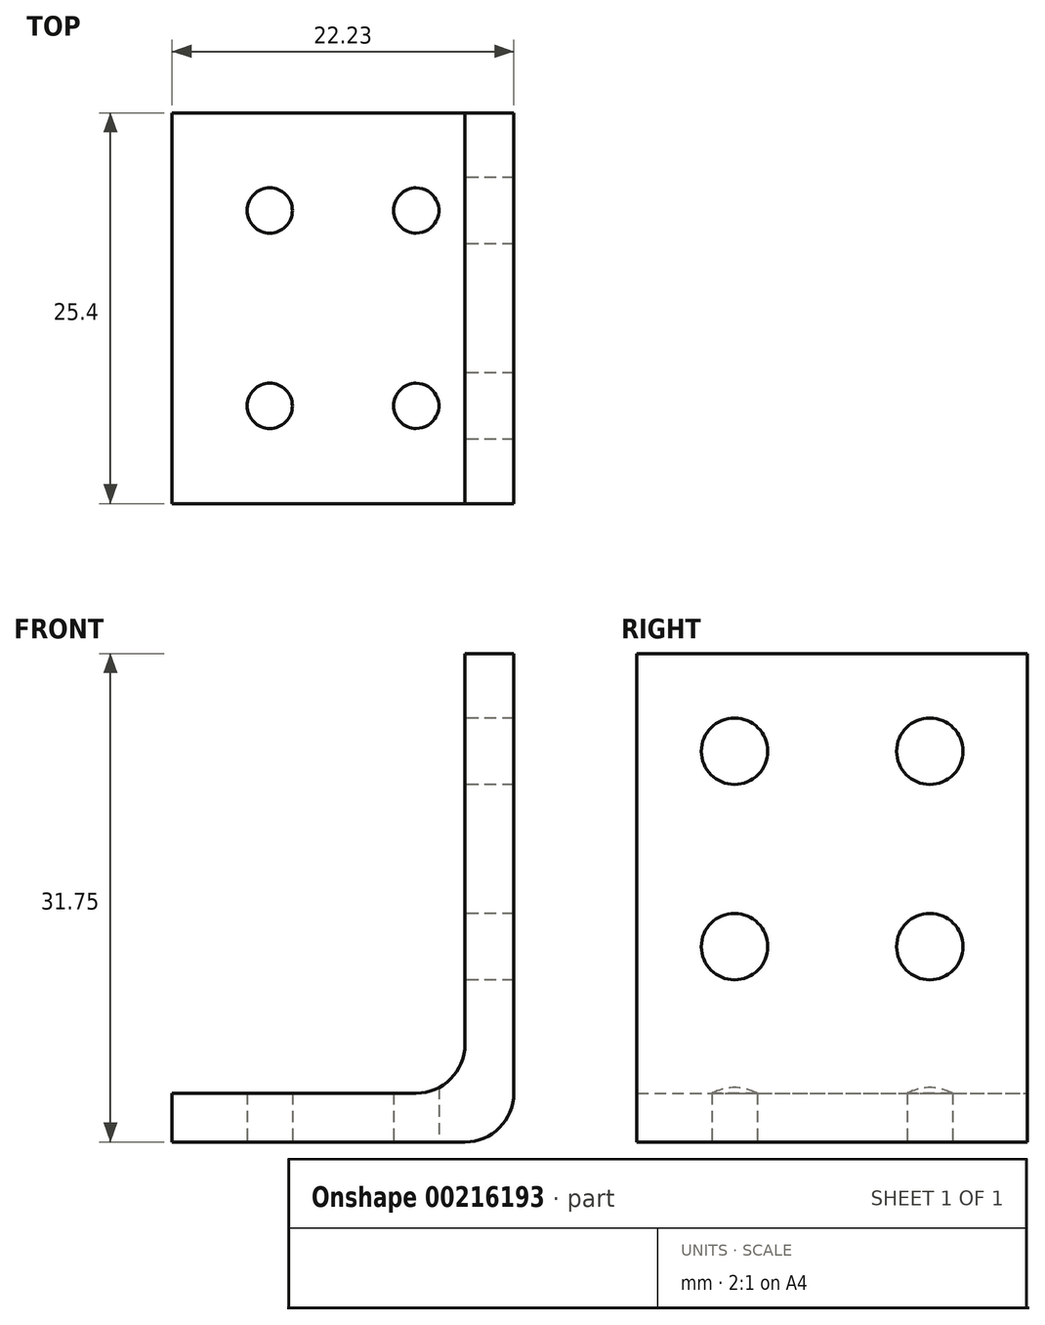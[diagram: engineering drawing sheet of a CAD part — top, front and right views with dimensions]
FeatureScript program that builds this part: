
annotation { "Feature Type Name" : "Feature", "Feature Type Description" : "" }
export const myFeature = defineFeature(function(context is Context, id is Id, definition is map)
    precondition{}
    {
        {
            var Q0;
            Q0=qCreatedBy(makeId("Front.planeOp"),FACE);
            var sketch = newSketch(context, id + "F0", { "sketchPlane" : qUnion([Q0])});
            skLineSegment(sketch, "E0", {"start": v(0, 3.18) * mm, "end": v(0, 31.75) * mm});
            skLineSegment(sketch, "E1", {"start": v(0, 31.75) * mm, "end": v(-3.17, 31.75) * mm});
            skLineSegment(sketch, "E2", {"start": v(-3.17, 31.75) * mm, "end": v(-3.17, 6.35) * mm});
            skLineSegment(sketch, "E3", {"start": v(-6.35, 3.17) * mm, "end": v(-22.22, 3.17) * mm});
            skLineSegment(sketch, "E4", {"start": v(-22.22, 3.17) * mm, "end": v(-22.22, 0) * mm});
            skLineSegment(sketch, "E5", {"start": v(-22.22, 0) * mm, "end": v(-3.17, 0) * mm});
            skPoint(sketch, "E6.visualSharp", {"position": v(-3.17, 3.17) * mm});
            skArc(sketch, "E6.filletArc", {"start": v(-6.35, 3.17) * mm, "mid": v(-4.1, 4.1) * mm, "end": v(-3.17, 6.35) * mm});
            skPoint(sketch, "E7.visualSharp", {"position": v(0, 0) * mm});
            skArc(sketch, "E7.filletArc", {"start": v(-3.17, 0) * mm, "mid": v(-0.93, 0.93) * mm, "end": v(0, 3.18) * mm});
            skSolve(sketch);
        }
        {
            var Q0;
            Q0=makeQuery(id+"F0.imprint","IMPRINT",FACE,{"disambiguationData":[TD([[makeQuery(id+"F0.imprint","IMPRINT",EDGE,{"derivedFrom":sQuery(id+"F0.wireOp",EDGE,"E0")}),1.0]])]});
            extrude(context, id + "F1", {"entities" : qUnion([Q0]), "depth" : 25.4 * mm});
        }
        {
            var Q0;
            Q0=makeQuery(id+"F1.opExtrude","SWEPT_FACE",FACE,{"disambiguationData":[OSD([sQuery(id+"F0.wireOp",EDGE,"E2")])]});
            var sketch = newSketch(context, id + "F2", { "sketchPlane" : qUnion([Q0])});
            skLineSegment(sketch, "E8", {"start": v(12.7, 31.75) * mm, "end": v(12.7, 19.05) * mm});
            skLineSegment(sketch, "E9.bottom", {"start": v(19.05, 12.7) * mm, "end": v(6.35, 12.7) * mm});
            skLineSegment(sketch, "E9.top", {"start": v(19.05, 25.4) * mm, "end": v(6.35, 25.4) * mm});
            skLineSegment(sketch, "E9.left", {"start": v(19.05, 12.7) * mm, "end": v(19.05, 25.4) * mm});
            skLineSegment(sketch, "E9.right", {"start": v(6.35, 12.7) * mm, "end": v(6.35, 25.4) * mm});
            skPoint(sketch, "E9.middle", {"position": v(12.7, 19.05) * mm});
            skSolve(sketch);
        }
        {
            var Q0;
            Q0=sQuery(id+"F2.wireOp",VERTEX,"E9.bottom.end");
            var Q1;
            Q1=sQuery(id+"F2.wireOp",VERTEX,"E9.top.end");
            var Q2;
            Q2=sQuery(id+"F2.wireOp",VERTEX,"E9.top.start");
            var Q3;
            Q3=sQuery(id+"F2.wireOp",VERTEX,"E9.left.start");
            var Q4;
            Q4=makeQuery(id+"F1.opExtrude","SWEPT_BODY",BODY,{"disambiguationData":[OSD([sQuery(id+"F0.wireOp",EDGE,"E0"),sQuery(id+"F0.wireOp",EDGE,"E1"),sQuery(id+"F0.wireOp",EDGE,"E2"),sQuery(id+"F0.wireOp",EDGE,"E3"),sQuery(id+"F0.wireOp",EDGE,"E4"),sQuery(id+"F0.wireOp",EDGE,"E5"),sQuery(id+"F0.wireOp",EDGE,"E6.filletArc"),sQuery(id+"F0.wireOp",EDGE,"E7.filletArc")])]});
            hole(context, id + "F3", {"style" : HoleStyle.SIMPLE, "endStyle" : HoleEndStyle.BLIND, "standardTappedOrClearance" : lookupTablePath({ "standard" : "ANSI", "fit" : "Close", "size" : "#8", "type" : "Clearance" }), "standardBlindInLast" : lookupTablePath({ "fit" : "Close", "standard" : "ANSI", "size" : "#8", "type" : "Clearance" }), "holeDiameter" : 4.32 * mm, "holeDepth" : 5.08 * mm, "locations" : qUnion([Q0, Q1, Q2, Q3]), "scope" : qUnion([Q4])});
        }
        {
            var Q0;
            Q0=makeQuery(id+"F1.opExtrude","SWEPT_FACE",FACE,{"disambiguationData":[OSD([sQuery(id+"F0.wireOp",EDGE,"E5")])]});
            var sketch = newSketch(context, id + "F4", { "sketchPlane" : qUnion([Q0])});
            skLineSegment(sketch, "E10", {"start": v(0, 0) * mm, "end": v(0, 12.7) * mm});
            skLineSegment(sketch, "E11", {"start": v(0, 12.7) * mm, "end": v(-6.35, 12.7) * mm});
            skPoint(sketch, "E11.endSnap0", {"position": v(-3.17, 12.7) * mm});
            skLineSegment(sketch, "E12", {"start": v(-6.35, 12.7) * mm, "end": v(-6.35, 19.05) * mm});
            skLineSegment(sketch, "E13", {"start": v(-6.35, 19.05) * mm, "end": v(-15.88, 19.05) * mm});
            skLineSegment(sketch, "E14", {"start": v(-15.88, 19.05) * mm, "end": v(-15.88, 6.35) * mm});
            skLineSegment(sketch, "E15", {"start": v(-15.88, 6.35) * mm, "end": v(-6.35, 6.35) * mm});
            skSolve(sketch);
        }
        {
            var Q0;
            Q0=sQuery(id+"F4.wireOp",VERTEX,"E15.end");
            var Q1;
            Q1=sQuery(id+"F4.wireOp",VERTEX,"E13.start");
            var Q2;
            Q2=sQuery(id+"F4.wireOp",VERTEX,"E14.start");
            var Q3;
            Q3=sQuery(id+"F4.wireOp",VERTEX,"E15.start");
            var Q4;
            Q4=makeQuery(id+"F1.opExtrude","SWEPT_BODY",BODY,{"disambiguationData":[OSD([sQuery(id+"F0.wireOp",EDGE,"E0"),sQuery(id+"F0.wireOp",EDGE,"E1"),sQuery(id+"F0.wireOp",EDGE,"E2"),sQuery(id+"F0.wireOp",EDGE,"E3"),sQuery(id+"F0.wireOp",EDGE,"E4"),sQuery(id+"F0.wireOp",EDGE,"E5"),sQuery(id+"F0.wireOp",EDGE,"E6.filletArc"),sQuery(id+"F0.wireOp",EDGE,"E7.filletArc")])]});
            hole(context, id + "F5", {"style" : HoleStyle.SIMPLE, "endStyle" : HoleEndStyle.BLIND, "standardTappedOrClearance" : lookupTablePath({ "standard" : "ANSI", "fit" : "Close", "size" : "#4", "type" : "Clearance" }), "standardBlindInLast" : lookupTablePath({ "fit" : "Close", "standard" : "ANSI", "size" : "#4", "type" : "Clearance" }), "holeDiameter" : 2.95 * mm, "holeDepth" : 5.08 * mm, "locations" : qUnion([Q0, Q1, Q2, Q3]), "scope" : qUnion([Q4])});
        }
    });
